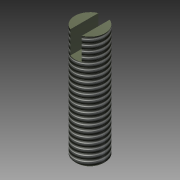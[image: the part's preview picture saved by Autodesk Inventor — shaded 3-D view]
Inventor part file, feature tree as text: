
AUTODESK INVENTOR PART (.ipt)
format: ipt  version: 2015 (Build 190159000, 159)  size: 97,792 bytes
history: native  units: mm
features: extrude x2, sketch x2, thread x1, chamfer x1
ambient origin geometry x8: Origin, YZ Plane, XZ Plane, XY Plane, X Axis, Y Axis, Z Axis, Center Point
bodies: 实体1 (feature_tree)
feature tree (6):
  extrude  "拉伸1"  Depth=15.0mm TaperAngle=0.0deg
  extrude  "拉伸2"  Depth=3.0mm TaperAngle=0.0deg
  thread  "螺纹1"  [1 undecoded]
  chamfer  "倒角1"  Distance=2.0mm Angle=45.0deg
  sketch  "草图1"  dims[d0=4.0mm d1=15.0mm d2=0.0mm]
  sketch  "草图2"  dims[d3=1.5mm d4=3.0mm d5=0.0mm d6=10.0mm d7=0.0mm d8=0.25mm d9=2.0mm d10=45.0deg]
note: 1 required parameter value undecoded (feature->parameter linkage not recoverable at this tier; creation-order binding heuristic only, values carry confidence <= 0.55)
